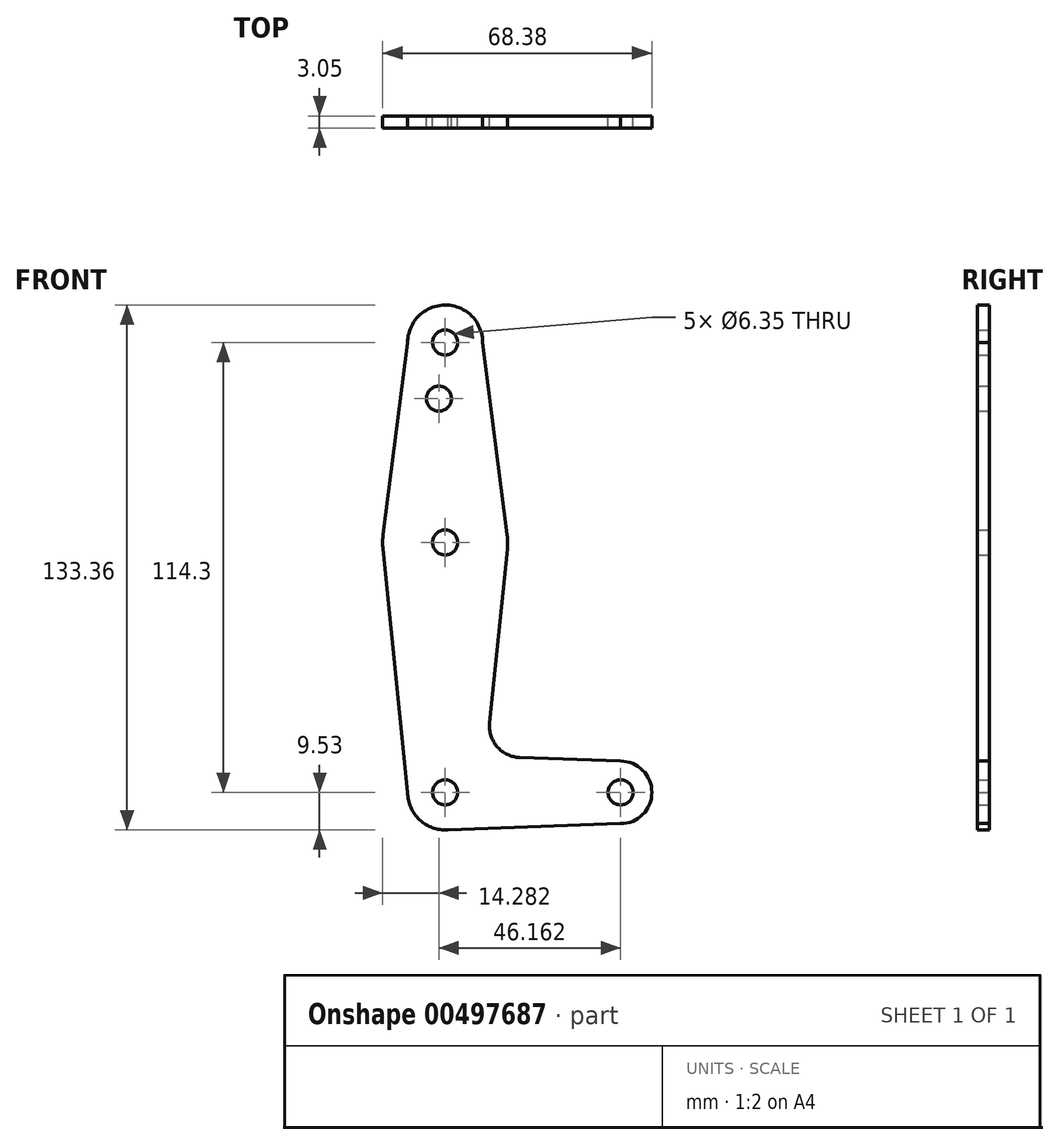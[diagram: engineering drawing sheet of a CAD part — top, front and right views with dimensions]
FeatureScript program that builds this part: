
annotation { "Feature Type Name" : "Feature", "Feature Type Description" : "" }
export const myFeature = defineFeature(function(context is Context, id is Id, definition is map)
    precondition{}
    {
        {
            var Q0;
            Q0=qCreatedBy(makeId("Front.planeOp"),FACE);
            var sketch = newSketch(context, id + "F0", { "sketchPlane" : qUnion([Q0])});
            skLineSegment(sketch, "E0", {"start": v(0, 0) * mm, "end": v(44.57, 0) * mm, "construction": true});
            skLineSegment(sketch, "E1", {"start": v(0, 0) * mm, "end": v(0, 63.5) * mm, "construction": true});
            skLineSegment(sketch, "E2", {"start": v(0, 63.5) * mm, "end": v(0, 114.3) * mm, "construction": true});
            skCircle(sketch, "E3", {"center": v(0, 114.3) * mm, "radius": 9.53 * mm});
            skCircle(sketch, "E4", {"center": v(0, 0) * mm, "radius": 9.53 * mm});
            skCircle(sketch, "E5", {"center": v(0, 63.5) * mm, "radius": 15.88 * mm});
            skCircle(sketch, "E6", {"center": v(44.57, 0) * mm, "radius": 7.94 * mm});
            skLineSegment(sketch, "E7", {"start": v(-9.52, 114.12) * mm, "end": v(-15.75, 65.52) * mm});
            skLineSegment(sketch, "E8", {"start": v(9.52, 114.3) * mm, "end": v(15.75, 65.52) * mm});
            skLineSegment(sketch, "E9", {"start": v(-9.53, 0) * mm, "end": v(-15.8, 61.9) * mm});
            skLineSegment(sketch, "E10", {"start": v(11.3, 17.6) * mm, "end": v(15.8, 61.9) * mm});
            skLineSegment(sketch, "E11", {"start": v(0, -9.52) * mm, "end": v(44.57, -7.94) * mm});
            skLineSegment(sketch, "E12", {"start": v(44.57, 7.94) * mm, "end": v(18.93, 8.85) * mm});
            skCircle(sketch, "E13", {"center": v(0, 114.3) * mm, "radius": 3.18 * mm});
            skCircle(sketch, "E14", {"center": v(0, 63.5) * mm, "radius": 3.18 * mm});
            skCircle(sketch, "E15", {"center": v(0, 0) * mm, "radius": 3.18 * mm});
            skCircle(sketch, "E16", {"center": v(44.57, 0) * mm, "radius": 3.18 * mm});
            skCircle(sketch, "E17", {"center": v(-1.59, 100.03) * mm, "radius": 3.18 * mm});
            skArc(sketch, "E18.filletArc", {"start": v(11.3, 17.6) * mm, "mid": v(13.22, 11.57) * mm, "end": v(18.93, 8.85) * mm});
            skSolve(sketch);
        }
        {
            var Q0;
            Q0 = qSketchRegion(id + "F0", true);
            extrude(context, id + "F1", {"entities" : qUnion([Q0]), "depth" : 3.05 * mm});
        }
    });
